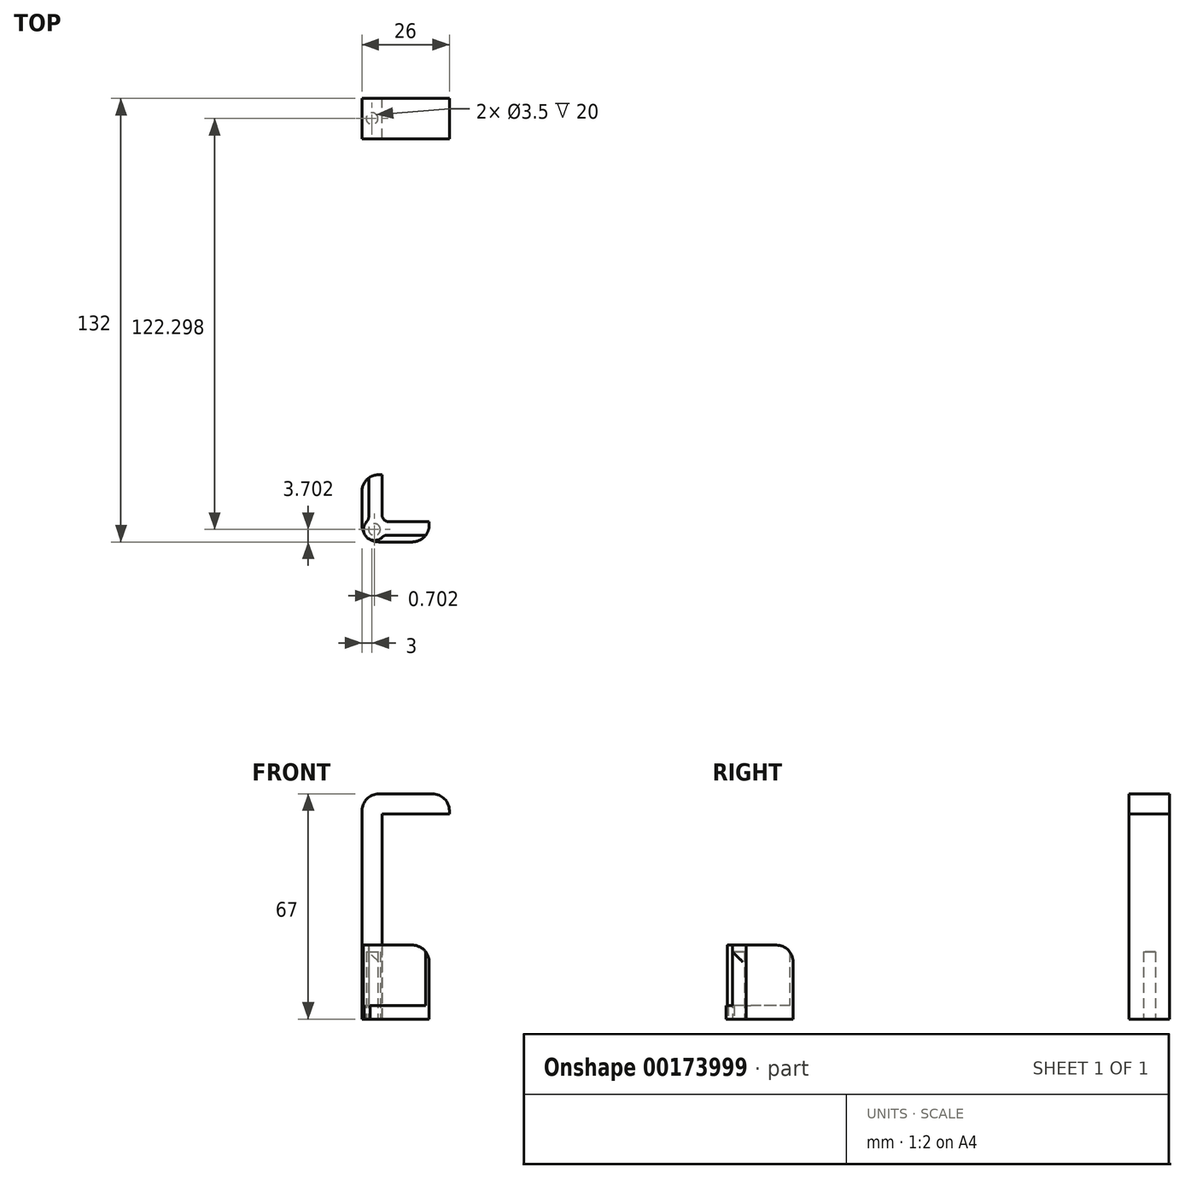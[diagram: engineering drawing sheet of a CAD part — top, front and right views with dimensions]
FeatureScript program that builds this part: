
annotation { "Feature Type Name" : "Feature", "Feature Type Description" : "" }
export const myFeature = defineFeature(function(context is Context, id is Id, definition is map)
    precondition{}
    {
        {
            assignVariable(context, id + "F0", {"name" : "wall", "anyValue" : 6});
        }
        {
            assignVariable(context, id + "F1", {"name" : "thickness", "anyValue" : 4});
        }
        {
            assignVariable(context, id + "F2", {"name" : "filletMajor", "anyValue" : 5});
        }
        {
            assignVariable(context, id + "F3", {"name" : "filletMinor", "anyValue" : 2});
        }
        {
            var Q0;
            Q0=qCreatedBy(makeId("Top.planeOp"),FACE);
            var sketch = newSketch(context, id + "F4", { "sketchPlane" : qUnion([Q0])});
            skLineSegment(sketch, "E0", {"start": v(0, 0) * mm, "end": v(20, 0) * mm});
            skLineSegment(sketch, "E1", {"start": v(20, 0) * mm, "end": v(20, 6) * mm});
            skLineSegment(sketch, "E2", {"start": v(20, 6) * mm, "end": v(6, 6) * mm});
            skLineSegment(sketch, "E3", {"start": v(6, 6) * mm, "end": v(6, 20) * mm});
            skLineSegment(sketch, "E4", {"start": v(6, 20) * mm, "end": v(0, 20) * mm});
            skLineSegment(sketch, "E5", {"start": v(0, 20) * mm, "end": v(0, 0) * mm});
            skSolve(sketch);
        }
        {
            var Q0;
            Q0 = qSketchRegion(id + "F4", true);
            extrude(context, id + "F5", {"entities" : qUnion([Q0]), "depth" : (getVariable(context, 'thickness')) * mm});
        }
        {
            var Q0;
            Q0=makeQuery(id+"F5.opExtrude","CAP_FACE",FACE,{"disambiguationData":[OSD([sQuery(id+"F4.wireOp",EDGE,"E0"),sQuery(id+"F4.wireOp",EDGE,"E1"),sQuery(id+"F4.wireOp",EDGE,"E2"),sQuery(id+"F4.wireOp",EDGE,"E3"),sQuery(id+"F4.wireOp",EDGE,"E4"),sQuery(id+"F4.wireOp",EDGE,"E5")])],"isStart":false});
            var sketch = newSketch(context, id + "F6", { "sketchPlane" : qUnion([Q0])});
            skLineSegment(sketch, "E6.0", {"start": v(6, 6) * mm, "end": v(6, 20) * mm});
            skLineSegment(sketch, "E6.1", {"start": v(20, 6) * mm, "end": v(6, 6) * mm});
            skLineSegment(sketch, "E7", {"start": v(6, 20) * mm, "end": v(2, 20) * mm});
            skLineSegment(sketch, "E8", {"start": v(2, 20) * mm, "end": v(2, 2) * mm});
            skLineSegment(sketch, "E9", {"start": v(2, 2) * mm, "end": v(20, 2) * mm});
            skLineSegment(sketch, "E10", {"start": v(20, 6) * mm, "end": v(20, 2) * mm});
            skSolve(sketch);
        }
        {
            var Q0;
            Q0 = qSketchRegion(id + "F6", true);
            extrude(context, id + "F7", {"entities" : qUnion([Q0]), "operationType" : NewBodyOperationType.ADD, "depth" : 18 * mm});
        }
        {
            var Q0;
            Q0=makeQuery(id+"F7.opExtrude","CAP_EDGE",EDGE,{"disambiguationData":[OSD([sQuery(id+"F6.wireOp",EDGE,"E7")])],"isStart":false});
            var Q1;
            Q1=makeQuery(id+"F7.opExtrude","CAP_EDGE",EDGE,{"disambiguationData":[OSD([sQuery(id+"F6.wireOp",EDGE,"E10")])],"isStart":false});
            var Q2;
            Q2=makeQuery(id+"F7.opExtrude","SWEPT_EDGE",EDGE,{"disambiguationData":[OSD([sQuery(id+"F6.wireOp",EDGE,"E8"),sQuery(id+"F6.wireOp",EDGE,"E9")])]});
            var Q3;
            Q3=makeQuery(id+"F5.opExtrude","SWEPT_EDGE",EDGE,{"disambiguationData":[OSD([sQuery(id+"F4.wireOp",EDGE,"E0"),sQuery(id+"F4.wireOp",EDGE,"E1")])]});
            var Q4;
            Q4=makeQuery(id+"F5.opExtrude","SWEPT_EDGE",EDGE,{"disambiguationData":[OSD([sQuery(id+"F4.wireOp",EDGE,"E4"),sQuery(id+"F4.wireOp",EDGE,"E5")])]});
            var Q5;
            Q5=makeQuery(id+"F5.opExtrude","SWEPT_EDGE",EDGE,{"disambiguationData":[OSD([sQuery(id+"F4.wireOp",EDGE,"E0"),sQuery(id+"F4.wireOp",EDGE,"E5")])]});
            fillet(context, id + "F8", {"entities" : qUnion([Q0, Q1, Q2, Q3, Q4, Q5]), "radius" : (getVariable(context, 'filletMajor')) * mm, "tangentPropagation" : true, "allowEdgeOverflow" : false});
        }
        {
            var Q0;
            Q0=makeQuery(id+"F5.opExtrude","CAP_FACE",FACE,{"disambiguationData":[OSD([sQuery(id+"F4.wireOp",EDGE,"E0"),sQuery(id+"F4.wireOp",EDGE,"E1"),sQuery(id+"F4.wireOp",EDGE,"E2"),sQuery(id+"F4.wireOp",EDGE,"E3"),sQuery(id+"F4.wireOp",EDGE,"E4"),sQuery(id+"F4.wireOp",EDGE,"E5")])],"isStart":true});
            var sketch = newSketch(context, id + "F9", { "sketchPlane" : qUnion([Q0])});
            skCircle(sketch, "E11", {"center": v(3.7, -3.7) * mm, "radius": 3.25 * mm});
            skLineSegment(sketch, "E12", {"start": v(6, -6) * mm, "end": v(1.46, -1.46) * mm, "construction": true});
            skSolve(sketch);
        }
        {
            var Q0;
            Q0 = qSketchRegion(id + "F9", true);
            var Q1;
            Q1=makeQuery(id+"F7.opExtrude","CAP_FACE",FACE,{"disambiguationData":[OSD([sQuery(id+"F6.wireOp",EDGE,"E6.0"),sQuery(id+"F6.wireOp",EDGE,"E6.1"),sQuery(id+"F6.wireOp",EDGE,"E7"),sQuery(id+"F6.wireOp",EDGE,"E8"),sQuery(id+"F6.wireOp",EDGE,"E9"),sQuery(id+"F6.wireOp",EDGE,"E10")])],"isStart":false});
            extrude(context, id + "F10", {"entities" : qUnion([Q0]), "operationType" : NewBodyOperationType.ADD, "endBound" : BoundingType.UP_TO_SURFACE, "oppositeDirection" : true, "endBoundEntityFace" : qUnion([Q1]), "depth" : 20 * mm});
        }
        {
            var Q0;
            Q0=makeQuery(id+"F5.opExtrude","CAP_FACE",FACE,{"disambiguationData":[OSD([sQuery(id+"F4.wireOp",EDGE,"E0"),sQuery(id+"F4.wireOp",EDGE,"E1"),sQuery(id+"F4.wireOp",EDGE,"E2"),sQuery(id+"F4.wireOp",EDGE,"E3"),sQuery(id+"F4.wireOp",EDGE,"E4"),sQuery(id+"F4.wireOp",EDGE,"E5")])],"isStart":true});
            var sketch = newSketch(context, id + "F11", { "sketchPlane" : qUnion([Q0])});
            skCircle(sketch, "E13", {"center": v(3.7, -3.7) * mm, "radius": 1.75 * mm});
            skSolve(sketch);
        }
        {
            var Q0;
            Q0 = qSketchRegion(id + "F11", true);
            extrude(context, id + "F12", {"entities" : qUnion([Q0]), "operationType" : NewBodyOperationType.REMOVE, "oppositeDirection" : true, "depth" : 20 * mm});
        }
        {
            var Q0;
            Q0=makeQuery(id+"F10.boolean.opBoolean","INTERSECT",EDGE,{"disambiguationData":[OD(0.0)],"derivedFrom":[makeQuery(id+"F8.opFillet","BLEND_FACE",FACE,{"disambiguationData":[OSD([sQuery(id+"F6.wireOp",EDGE,"E8"),sQuery(id+"F6.wireOp",EDGE,"E9")])]}),makeQuery(id+"F10.opExtrude","SWEPT_FACE",FACE,{"disambiguationData":[OSD([sQuery(id+"F9.wireOp",EDGE,"E11")])]})]});
            var Q1;
            Q1=makeQuery(id+"F10.boolean.opBoolean","INTERSECT",EDGE,{"disambiguationData":[OD(1.0)],"derivedFrom":[makeQuery(id+"F8.opFillet","BLEND_FACE",FACE,{"disambiguationData":[OSD([sQuery(id+"F6.wireOp",EDGE,"E8"),sQuery(id+"F6.wireOp",EDGE,"E9")])]}),makeQuery(id+"F10.opExtrude","SWEPT_FACE",FACE,{"disambiguationData":[OSD([sQuery(id+"F9.wireOp",EDGE,"E11")])]})]});
            var Q2;
            Q2=makeQuery(id+"F7.boolean.opBoolean","MERGE",EDGE,{"derivedFrom":[makeQuery(id+"F5.opExtrude","SWEPT_EDGE",EDGE,{"disambiguationData":[OSD([sQuery(id+"F4.wireOp",EDGE,"E2"),sQuery(id+"F4.wireOp",EDGE,"E3")])]}),makeQuery(id+"F7.opExtrude","SWEPT_EDGE",EDGE,{"disambiguationData":[OSD([sQuery(id+"F6.wireOp",EDGE,"E6.0"),sQuery(id+"F6.wireOp",EDGE,"E6.1")])]})]});
            fillet(context, id + "F13", {"entities" : qUnion([Q0, Q1, Q2]), "radius" : (getVariable(context, 'filletMinor')) * mm, "tangentPropagation" : true, "allowEdgeOverflow" : false});
        }
        {
            var Q0;
            Q0=makeQuery(id+"F7.boolean.opBoolean","MERGE",FACE,{"derivedFrom":[makeQuery(id+"F5.opExtrude","SWEPT_FACE",FACE,{"disambiguationData":[OSD([sQuery(id+"F4.wireOp",EDGE,"E3")])]}),makeQuery(id+"F7.opExtrude","SWEPT_FACE",FACE,{"disambiguationData":[OSD([sQuery(id+"F6.wireOp",EDGE,"E6.0")])]})]});
            var sketch = newSketch(context, id + "F14", { "sketchPlane" : qUnion([Q0])});
            skLineSegment(sketch, "E14.bottom", {"start": v(120, 0) * mm, "end": v(132, 0) * mm});
            skLineSegment(sketch, "E14.top", {"start": v(120, 61) * mm, "end": v(132, 61) * mm});
            skLineSegment(sketch, "E14.left", {"start": v(120, 0) * mm, "end": v(120, 61) * mm});
            skLineSegment(sketch, "E14.right", {"start": v(132, 0) * mm, "end": v(132, 61) * mm});
            skSolve(sketch);
        }
        {
            var Q0;
            Q0 = qSketchRegion(id + "F14", true);
            extrude(context, id + "F15", {"entities" : qUnion([Q0]), "oppositeDirection" : true, "depth" : (getVariable(context, 'wall')) * mm});
        }
        {
            var Q0;
            Q0=makeQuery(id+"F15.opExtrude","SWEPT_FACE",FACE,{"disambiguationData":[OSD([sQuery(id+"F14.wireOp",EDGE,"E14.top")])]});
            var sketch = newSketch(context, id + "F16", { "sketchPlane" : qUnion([Q0])});
            skLineSegment(sketch, "E15.bottom", {"start": v(0, 132) * mm, "end": v(26, 132) * mm});
            skLineSegment(sketch, "E15.top", {"start": v(0, 120) * mm, "end": v(26, 120) * mm});
            skLineSegment(sketch, "E15.left", {"start": v(0, 132) * mm, "end": v(0, 120) * mm});
            skLineSegment(sketch, "E15.right", {"start": v(26, 132) * mm, "end": v(26, 120) * mm});
            skSolve(sketch);
        }
        {
            var Q0;
            Q0 = qSketchRegion(id + "F16", true);
            extrude(context, id + "F17", {"entities" : qUnion([Q0]), "operationType" : NewBodyOperationType.ADD, "depth" : (getVariable(context, 'wall')) * mm});
        }
        {
            var Q0;
            Q0=makeQuery(id+"F17.opExtrude","CAP_EDGE",EDGE,{"disambiguationData":[OSD([sQuery(id+"F16.wireOp",EDGE,"E15.left")])],"isStart":false});
            var Q1;
            Q1=makeQuery(id+"F17.opExtrude","CAP_EDGE",EDGE,{"disambiguationData":[OSD([sQuery(id+"F16.wireOp",EDGE,"E15.right")])],"isStart":false});
            fillet(context, id + "F18", {"entities" : qUnion([Q0, Q1]), "radius" : (getVariable(context, 'filletMajor')) * mm, "tangentPropagation" : true, "allowEdgeOverflow" : false});
        }
        {
            var Q0;
            Q0=makeQuery(id+"F15.opExtrude","SWEPT_FACE",FACE,{"disambiguationData":[OSD([sQuery(id+"F14.wireOp",EDGE,"E14.bottom")])]});
            var sketch = newSketch(context, id + "F19", { "sketchPlane" : qUnion([Q0])});
            skCircle(sketch, "E16", {"center": v(3, -126) * mm, "radius": 1.75 * mm});
            skPoint(sketch, "E16.centerSnap0", {"position": v(3, -120) * mm});
            skPoint(sketch, "E16.centerSnap1", {"position": v(0, -126) * mm});
            skSolve(sketch);
        }
        {
            var Q0;
            Q0 = qSketchRegion(id + "F19", true);
            extrude(context, id + "F20", {"entities" : qUnion([Q0]), "operationType" : NewBodyOperationType.REMOVE, "oppositeDirection" : true, "depth" : 20 * mm});
        }
    });
